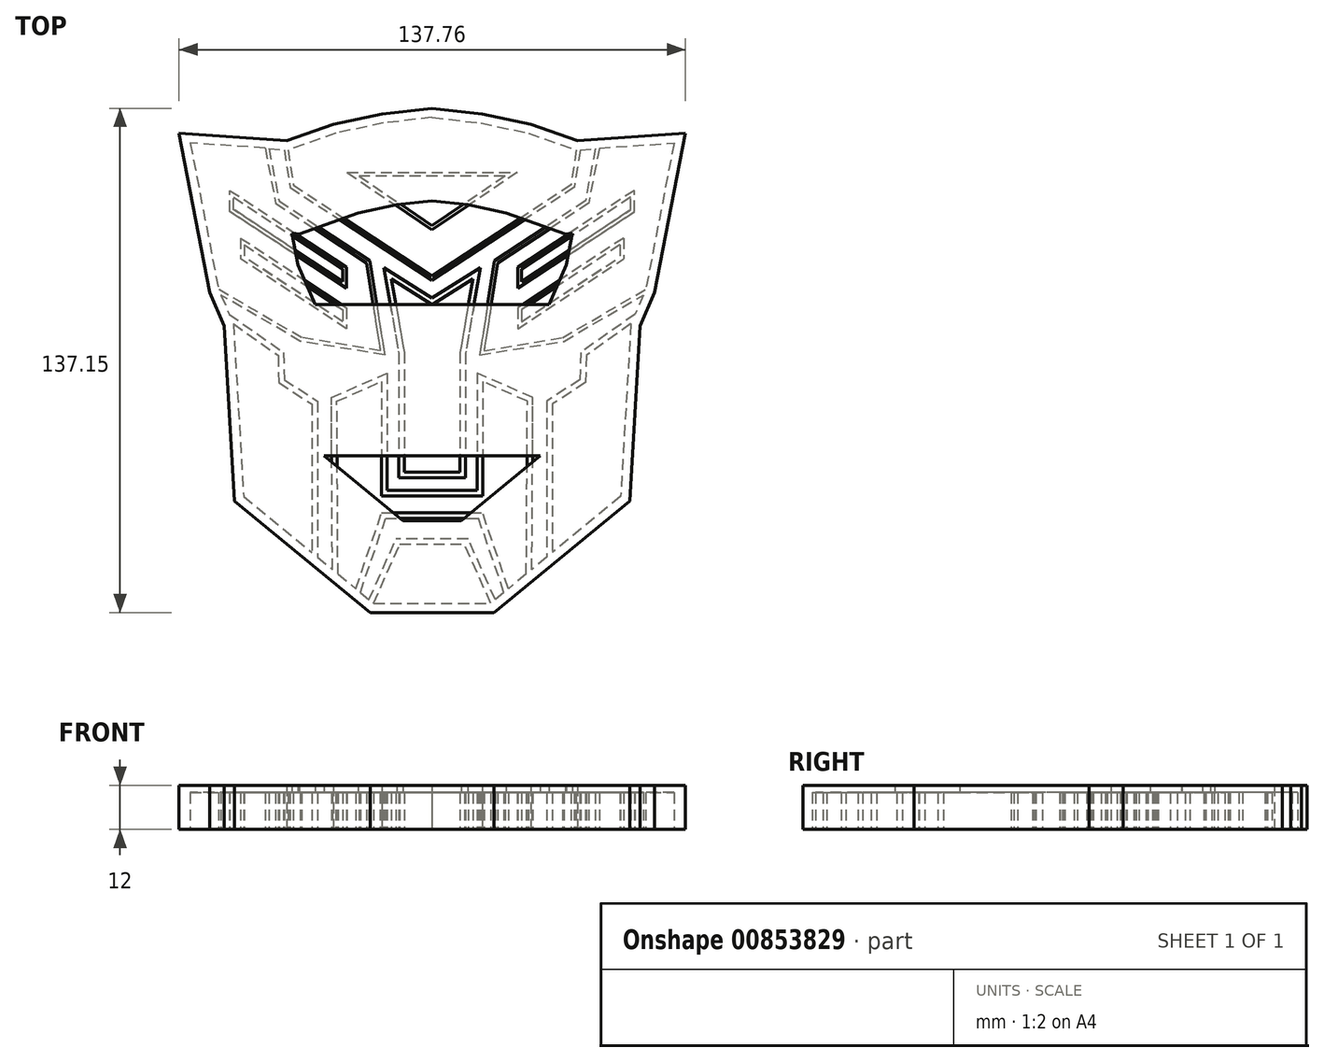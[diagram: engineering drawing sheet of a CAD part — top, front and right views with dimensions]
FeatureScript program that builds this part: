
annotation { "Feature Type Name" : "Feature", "Feature Type Description" : "" }
export const myFeature = defineFeature(function(context is Context, id is Id, definition is map)
    precondition{}
    {
        {
            var Q0;
            Q0=qCreatedBy(makeId("Top.planeOp"),FACE);
            cPlane(context, id + "F0", {"entities" : qUnion([Q0]), "cplaneType" : CPlaneType.OFFSET, "offset" : 2 * mm, "oppositeDirection" : true, "width" : 150 * mm, "height" : 150 * mm});
        }
        {
            var Q0;
            Q0=qCreatedBy(makeId("Top.planeOp"),FACE);
            var sketch = newSketch(context, id + "F1", { "sketchPlane" : qUnion([Q0])});
            skLineSegment(sketch, "E0", {"start": v(0, 70.5) * mm, "end": v(-13.27, 69) * mm});
            skLineSegment(sketch, "E1", {"start": v(-13.27, 69) * mm, "end": v(-26.23, 66.23) * mm});
            skLineSegment(sketch, "E2", {"start": v(-26.23, 66.23) * mm, "end": v(-39.24, 61.65) * mm});
            skLineSegment(sketch, "E3", {"start": v(-65.8, 63.53) * mm, "end": v(-58.11, 23.73) * mm});
            skLineSegment(sketch, "E4", {"start": v(-57.45, 22.2) * mm, "end": v(-55.2, 17) * mm});
            skLineSegment(sketch, "E5", {"start": v(-54.07, 14.36) * mm, "end": v(-51.3, -32.61) * mm});
            skLineSegment(sketch, "E6", {"start": v(-51.3, -32.61) * mm, "end": v(-32.74, -47.85) * mm});
            skLineSegment(sketch, "E7", {"start": v(-15.95, -61.64) * mm, "end": v(0, -61.64) * mm});
            skLineSegment(sketch, "E8.0", {"start": v(-16.84, -64.14) * mm, "end": v(0, -64.14) * mm});
            skLineSegment(sketch, "E8.1", {"start": v(-53.73, -33.85) * mm, "end": v(-16.84, -64.14) * mm});
            skLineSegment(sketch, "E8.2", {"start": v(-56.54, 13.77) * mm, "end": v(-53.73, -33.85) * mm});
            skLineSegment(sketch, "E8.3", {"start": v(-60.52, 23) * mm, "end": v(-56.54, 13.77) * mm});
            skLineSegment(sketch, "E8.4", {"start": v(-68.88, 66.25) * mm, "end": v(-60.52, 23) * mm});
            skLineSegment(sketch, "E8.5", {"start": v(0, 73) * mm, "end": v(-13.67, 71.48) * mm});
            skLineSegment(sketch, "E8.6", {"start": v(-13.67, 71.48) * mm, "end": v(-26.91, 68.64) * mm});
            skLineSegment(sketch, "E8.7", {"start": v(-26.91, 68.64) * mm, "end": v(-39.6, 64.17) * mm});
            skLineSegment(sketch, "E8.8", {"start": v(-39.6, 64.17) * mm, "end": v(-68.88, 66.25) * mm});
            skLineSegment(sketch, "E9", {"start": v(0, 55.54) * mm, "end": v(-23.13, 55.54) * mm});
            skLineSegment(sketch, "E10", {"start": v(-23.13, 55.54) * mm, "end": v(0, 39.93) * mm});
            skLineSegment(sketch, "E11.0", {"start": v(-19.86, 54.54) * mm, "end": v(0, 41.13) * mm});
            skLineSegment(sketch, "E11.1", {"start": v(0, 54.54) * mm, "end": v(-19.86, 54.54) * mm});
            skLineSegment(sketch, "E12", {"start": v(-39.24, 61.65) * mm, "end": v(-37.75, 52.11) * mm});
            skLineSegment(sketch, "E13", {"start": v(-37.75, 52.11) * mm, "end": v(0, 27.37) * mm});
            skLineSegment(sketch, "E14.0", {"start": v(-38.67, 51.52) * mm, "end": v(0, 26.18) * mm});
            skLineSegment(sketch, "E14.1", {"start": v(-40.26, 61.7) * mm, "end": v(-38.67, 51.52) * mm});
            skLineSegment(sketch, "E15", {"start": v(-45.46, 62.21) * mm, "end": v(-42.55, 47.16) * mm});
            skLineSegment(sketch, "E16", {"start": v(-42.55, 47.16) * mm, "end": v(-17.9, 30.94) * mm});
            skLineSegment(sketch, "E17", {"start": v(-17.9, 30.94) * mm, "end": v(-14.13, 7.11) * mm});
            skLineSegment(sketch, "E18", {"start": v(-14.13, 7.11) * mm, "end": v(-35.49, 10.61) * mm});
            skLineSegment(sketch, "E19", {"start": v(-35.49, 10.61) * mm, "end": v(-58.11, 23.73) * mm});
            skLineSegment(sketch, "E20.0", {"start": v(-35.83, 9.65) * mm, "end": v(-57.45, 22.2) * mm});
            skLineSegment(sketch, "E20.1", {"start": v(-44.4, 62) * mm, "end": v(-41.65, 47.76) * mm});
            skLineSegment(sketch, "E20.2", {"start": v(-41.65, 47.76) * mm, "end": v(-16.99, 31.54) * mm});
            skLineSegment(sketch, "E20.3", {"start": v(-16.99, 31.54) * mm, "end": v(-12.93, 5.9) * mm});
            skLineSegment(sketch, "E20.4", {"start": v(-12.93, 5.9) * mm, "end": v(-35.83, 9.65) * mm});
            skLineSegment(sketch, "E21", {"start": v(-54.07, 14.36) * mm, "end": v(-41.9, 5.77) * mm});
            skLineSegment(sketch, "E22", {"start": v(-41.9, 5.77) * mm, "end": v(-41.72, -1.6) * mm});
            skLineSegment(sketch, "E23", {"start": v(-41.72, -1.6) * mm, "end": v(-32.74, -7.47) * mm});
            skLineSegment(sketch, "E24", {"start": v(-32.74, -7.47) * mm, "end": v(-32.74, -47.85) * mm});
            skLineSegment(sketch, "E25.0", {"start": v(-31.24, -6.66) * mm, "end": v(-31.24, -49.08) * mm});
            skLineSegment(sketch, "E25.1", {"start": v(-40.24, -0.78) * mm, "end": v(-31.24, -6.66) * mm});
            skLineSegment(sketch, "E25.2", {"start": v(-40.43, 6.56) * mm, "end": v(-40.24, -0.78) * mm});
            skLineSegment(sketch, "E25.3", {"start": v(-55.2, 17) * mm, "end": v(-40.43, 6.56) * mm});
            skLineSegment(sketch, "E26.trimOffspring", {"start": v(-45.46, 62.21) * mm, "end": v(-65.8, 63.53) * mm});
            skLineSegment(sketch, "E27.trimOffspring", {"start": v(-31.24, -49.08) * mm, "end": v(-27.14, -52.45) * mm});
            skLineSegment(sketch, "E28", {"start": v(-25.63, -53.69) * mm, "end": v(-25.92, -6.67) * mm});
            skLineSegment(sketch, "E29", {"start": v(-25.92, -6.67) * mm, "end": v(-13.73, -1.3) * mm});
            skLineSegment(sketch, "E30", {"start": v(-13.73, -1.3) * mm, "end": v(-13.73, -32.47) * mm});
            skLineSegment(sketch, "E31", {"start": v(-13.73, -32.47) * mm, "end": v(0, -32.47) * mm});
            skLineSegment(sketch, "E32", {"start": v(-20.78, -57.67) * mm, "end": v(-13.73, -37.08) * mm});
            skLineSegment(sketch, "E33", {"start": v(-13.73, -37.08) * mm, "end": v(0, -37.08) * mm});
            skLineSegment(sketch, "E34", {"start": v(-15.95, -61.64) * mm, "end": v(-8.81, -45.58) * mm});
            skLineSegment(sketch, "E35", {"start": v(-8.81, -45.58) * mm, "end": v(0, -45.58) * mm});
            skLineSegment(sketch, "E36.0", {"start": v(-12.23, -30.97) * mm, "end": v(0, -30.97) * mm});
            skLineSegment(sketch, "E36.1", {"start": v(-12.23, 1) * mm, "end": v(-12.23, -30.97) * mm});
            skLineSegment(sketch, "E36.2", {"start": v(-27.42, -5.7) * mm, "end": v(-12.23, 1) * mm});
            skLineSegment(sketch, "E36.3", {"start": v(-27.14, -52.45) * mm, "end": v(-27.42, -5.7) * mm});
            skLineSegment(sketch, "E37.0", {"start": v(-9.79, -44.08) * mm, "end": v(0, -44.08) * mm});
            skLineSegment(sketch, "E37.1", {"start": v(-17.15, -60.65) * mm, "end": v(-9.79, -44.08) * mm});
            skLineSegment(sketch, "E38.0", {"start": v(-12.66, -38.58) * mm, "end": v(0, -38.58) * mm});
            skLineSegment(sketch, "E38.1", {"start": v(-19.54, -58.69) * mm, "end": v(-12.66, -38.58) * mm});
            skLineSegment(sketch, "E39.trimOffspring", {"start": v(-25.63, -53.69) * mm, "end": v(-20.78, -57.67) * mm});
            skLineSegment(sketch, "E40.trimOffspring", {"start": v(-19.54, -58.69) * mm, "end": v(-17.15, -60.65) * mm});
            skLineSegment(sketch, "E41", {"start": v(0, 19.63) * mm, "end": v(-11.13, 26.56) * mm});
            skLineSegment(sketch, "E42", {"start": v(-11.13, 26.56) * mm, "end": v(-7.57, 6.56) * mm});
            skLineSegment(sketch, "E43", {"start": v(-7.57, 6.56) * mm, "end": v(-7.57, -25.95) * mm});
            skLineSegment(sketch, "E44", {"start": v(-7.57, -25.95) * mm, "end": v(0, -25.95) * mm});
            skLineSegment(sketch, "E45.0", {"start": v(-9.07, -27.45) * mm, "end": v(0, -27.45) * mm});
            skLineSegment(sketch, "E45.1", {"start": v(-9.07, 6.43) * mm, "end": v(-9.07, -27.45) * mm});
            skLineSegment(sketch, "E45.2", {"start": v(-13.2, 29.6) * mm, "end": v(-9.07, 6.43) * mm});
            skLineSegment(sketch, "E45.3", {"start": v(0, 21.4) * mm, "end": v(-13.2, 29.6) * mm});
            skLineSegment(sketch, "E46", {"start": v(-55.05, 50.68) * mm, "end": v(-23.28, 29.77) * mm});
            skLineSegment(sketch, "E47", {"start": v(-23.28, 29.77) * mm, "end": v(-23.28, 24.02) * mm});
            skLineSegment(sketch, "E48", {"start": v(-23.28, 24.02) * mm, "end": v(-55.05, 44.92) * mm});
            skLineSegment(sketch, "E49", {"start": v(-55.05, 44.92) * mm, "end": v(-55.05, 50.68) * mm});
            skLineSegment(sketch, "E50.0", {"start": v(-54.05, 45.46) * mm, "end": v(-54.05, 48.82) * mm});
            skLineSegment(sketch, "E50.1", {"start": v(-24.28, 25.87) * mm, "end": v(-54.05, 45.46) * mm});
            skLineSegment(sketch, "E50.2", {"start": v(-24.28, 29.23) * mm, "end": v(-24.28, 25.87) * mm});
            skLineSegment(sketch, "E50.3", {"start": v(-54.05, 48.82) * mm, "end": v(-24.28, 29.23) * mm});
            skLineSegment(sketch, "E51", {"start": v(-52.13, 37.73) * mm, "end": v(-23.28, 18.74) * mm});
            skLineSegment(sketch, "E52", {"start": v(-23.28, 18.74) * mm, "end": v(-23.28, 13.05) * mm});
            skLineSegment(sketch, "E53", {"start": v(-23.28, 13.05) * mm, "end": v(-52.13, 32.04) * mm});
            skLineSegment(sketch, "E54", {"start": v(-52.13, 37.73) * mm, "end": v(-52.13, 32.04) * mm});
            skLineSegment(sketch, "E55.0", {"start": v(-51.13, 35.87) * mm, "end": v(-51.13, 32.58) * mm});
            skLineSegment(sketch, "E55.1", {"start": v(-51.13, 35.87) * mm, "end": v(-24.28, 18.2) * mm});
            skLineSegment(sketch, "E55.2", {"start": v(-24.28, 18.2) * mm, "end": v(-24.28, 14.9) * mm});
            skLineSegment(sketch, "E55.3", {"start": v(-24.28, 14.9) * mm, "end": v(-51.13, 32.58) * mm});
            skLineSegment(sketch, "E56", {"start": v(0, 11.68) * mm, "end": v(0, -12.85) * mm, "construction": true});
            skLineSegment(sketch, "E57.MirrorCS", {"start": v(54.05, 45.46) * mm, "end": v(54.05, 48.82) * mm});
            skLineSegment(sketch, "E58.MirrorCS", {"start": v(51.13, 35.87) * mm, "end": v(51.13, 32.58) * mm});
            skLineSegment(sketch, "E59.MirrorCS", {"start": v(55.05, 44.92) * mm, "end": v(55.05, 50.68) * mm});
            skLineSegment(sketch, "E60.MirrorCS", {"start": v(31.24, -49.08) * mm, "end": v(27.14, -52.45) * mm});
            skLineSegment(sketch, "E61.MirrorCS", {"start": v(23.28, 29.77) * mm, "end": v(23.28, 24.02) * mm});
            skLineSegment(sketch, "E62.MirrorCS", {"start": v(52.13, 37.73) * mm, "end": v(52.13, 32.04) * mm});
            skLineSegment(sketch, "E63.MirrorCS", {"start": v(23.28, 18.74) * mm, "end": v(23.28, 13.05) * mm});
            skLineSegment(sketch, "E64.MirrorCS", {"start": v(57.45, 22.2) * mm, "end": v(55.2, 17) * mm});
            skLineSegment(sketch, "E65.MirrorCS", {"start": v(24.28, 29.23) * mm, "end": v(24.28, 25.87) * mm});
            skLineSegment(sketch, "E66.MirrorCS", {"start": v(19.54, -58.69) * mm, "end": v(17.15, -60.65) * mm});
            skLineSegment(sketch, "E67.MirrorCS", {"start": v(24.28, 18.2) * mm, "end": v(24.28, 14.9) * mm});
            skLineSegment(sketch, "E68.MirrorCS", {"start": v(39.24, 61.65) * mm, "end": v(37.75, 52.11) * mm});
            skLineSegment(sketch, "E69.MirrorCS", {"start": v(9.07, -27.45) * mm, "end": v(0, -27.45) * mm});
            skLineSegment(sketch, "E70.MirrorCS", {"start": v(17.9, 30.94) * mm, "end": v(14.13, 7.11) * mm});
            skLineSegment(sketch, "E71.MirrorCS", {"start": v(15.95, -61.64) * mm, "end": v(8.81, -45.58) * mm});
            skLineSegment(sketch, "E72.MirrorCS", {"start": v(17.15, -60.65) * mm, "end": v(9.79, -44.08) * mm});
            skLineSegment(sketch, "E73.MirrorCS", {"start": v(55.2, 17) * mm, "end": v(40.43, 6.56) * mm});
            skLineSegment(sketch, "E74.MirrorCS", {"start": v(42.55, 47.16) * mm, "end": v(17.9, 30.94) * mm});
            skLineSegment(sketch, "E75.MirrorCS", {"start": v(0, 70.5) * mm, "end": v(13.27, 69) * mm});
            skLineSegment(sketch, "E76.MirrorCS", {"start": v(26.91, 68.64) * mm, "end": v(39.6, 64.17) * mm});
            skLineSegment(sketch, "E77.MirrorCS", {"start": v(12.66, -38.58) * mm, "end": v(0, -38.58) * mm});
            skLineSegment(sketch, "E78.MirrorCS", {"start": v(25.63, -53.69) * mm, "end": v(25.92, -6.67) * mm});
            skLineSegment(sketch, "E79.MirrorCS", {"start": v(45.46, 62.21) * mm, "end": v(65.8, 63.53) * mm});
            skLineSegment(sketch, "E80.MirrorCS", {"start": v(0, 73) * mm, "end": v(13.67, 71.48) * mm});
            skLineSegment(sketch, "E81.MirrorCS", {"start": v(13.67, 71.48) * mm, "end": v(26.91, 68.64) * mm});
            skLineSegment(sketch, "E82.MirrorCS", {"start": v(8.81, -45.58) * mm, "end": v(0, -45.58) * mm});
            skLineSegment(sketch, "E83.MirrorCS", {"start": v(41.9, 5.77) * mm, "end": v(41.72, -1.6) * mm});
            skLineSegment(sketch, "E84.MirrorCS", {"start": v(35.49, 10.61) * mm, "end": v(58.11, 23.73) * mm});
            skLineSegment(sketch, "E85.MirrorCS", {"start": v(0, 54.54) * mm, "end": v(19.86, 54.54) * mm});
            skLineSegment(sketch, "E86.MirrorCS", {"start": v(24.28, 25.87) * mm, "end": v(54.05, 45.46) * mm});
            skLineSegment(sketch, "E87.MirrorCS", {"start": v(19.54, -58.69) * mm, "end": v(12.66, -38.58) * mm});
            skLineSegment(sketch, "E88.MirrorCS", {"start": v(25.92, -6.67) * mm, "end": v(13.73, -1.3) * mm});
            skLineSegment(sketch, "E89.MirrorCS", {"start": v(13.27, 69) * mm, "end": v(26.23, 66.23) * mm});
            skLineSegment(sketch, "E90.MirrorCS", {"start": v(41.72, -1.6) * mm, "end": v(32.74, -7.47) * mm});
            skLineSegment(sketch, "E91.MirrorCS", {"start": v(12.23, -30.97) * mm, "end": v(0, -30.97) * mm});
            skLineSegment(sketch, "E92.MirrorCS", {"start": v(26.23, 66.23) * mm, "end": v(39.24, 61.65) * mm});
            skLineSegment(sketch, "E93.MirrorCS", {"start": v(54.07, 14.36) * mm, "end": v(51.3, -32.61) * mm});
            skLineSegment(sketch, "E94.MirrorCS", {"start": v(27.14, -52.45) * mm, "end": v(27.42, -5.7) * mm});
            skLineSegment(sketch, "E95.MirrorCS", {"start": v(40.24, -0.78) * mm, "end": v(31.24, -6.66) * mm});
            skLineSegment(sketch, "E96.MirrorCS", {"start": v(39.6, 64.17) * mm, "end": v(68.88, 66.25) * mm});
            skLineSegment(sketch, "E97.MirrorCS", {"start": v(41.65, 47.76) * mm, "end": v(16.99, 31.54) * mm});
            skLineSegment(sketch, "E98.MirrorCS", {"start": v(9.07, 6.43) * mm, "end": v(9.07, -27.45) * mm});
            skLineSegment(sketch, "E99.MirrorCS", {"start": v(7.57, -25.95) * mm, "end": v(0, -25.95) * mm});
            skLineSegment(sketch, "E100.MirrorCS", {"start": v(14.13, 7.11) * mm, "end": v(35.49, 10.61) * mm});
            skLineSegment(sketch, "E101.MirrorCS", {"start": v(51.3, -32.61) * mm, "end": v(32.74, -47.85) * mm});
            skLineSegment(sketch, "E102.MirrorCS", {"start": v(23.13, 55.54) * mm, "end": v(0, 39.93) * mm});
            skLineSegment(sketch, "E103.MirrorCS", {"start": v(12.93, 5.9) * mm, "end": v(35.83, 9.65) * mm});
            skLineSegment(sketch, "E104.MirrorCS", {"start": v(40.43, 6.56) * mm, "end": v(40.24, -0.78) * mm});
            skLineSegment(sketch, "E105.MirrorCS", {"start": v(54.07, 14.36) * mm, "end": v(41.9, 5.77) * mm});
            skLineSegment(sketch, "E106.MirrorCS", {"start": v(9.79, -44.08) * mm, "end": v(0, -44.08) * mm});
            skLineSegment(sketch, "E107.MirrorCS", {"start": v(13.73, -37.08) * mm, "end": v(0, -37.08) * mm});
            skLineSegment(sketch, "E108.MirrorCS", {"start": v(19.86, 54.54) * mm, "end": v(0, 41.13) * mm});
            skLineSegment(sketch, "E109.MirrorCS", {"start": v(45.46, 62.21) * mm, "end": v(42.55, 47.16) * mm});
            skLineSegment(sketch, "E110.MirrorCS", {"start": v(23.28, 24.02) * mm, "end": v(55.05, 44.92) * mm});
            skLineSegment(sketch, "E111.MirrorCS", {"start": v(40.26, 61.7) * mm, "end": v(38.67, 51.52) * mm});
            skLineSegment(sketch, "E112.MirrorCS", {"start": v(16.84, -64.14) * mm, "end": v(0, -64.14) * mm});
            skLineSegment(sketch, "E113.MirrorCS", {"start": v(35.83, 9.65) * mm, "end": v(57.45, 22.2) * mm});
            skLineSegment(sketch, "E114.MirrorCS", {"start": v(25.63, -53.69) * mm, "end": v(20.78, -57.67) * mm});
            skLineSegment(sketch, "E115.MirrorCS", {"start": v(23.28, 13.05) * mm, "end": v(52.13, 32.04) * mm});
            skLineSegment(sketch, "E116.MirrorCS", {"start": v(65.8, 63.53) * mm, "end": v(58.11, 23.73) * mm});
            skLineSegment(sketch, "E117.MirrorCS", {"start": v(0, 19.63) * mm, "end": v(11.13, 26.56) * mm});
            skLineSegment(sketch, "E118.MirrorCS", {"start": v(0, 21.4) * mm, "end": v(13.2, 29.6) * mm});
            skLineSegment(sketch, "E119.MirrorCS", {"start": v(13.73, -1.3) * mm, "end": v(13.73, -32.47) * mm});
            skLineSegment(sketch, "E120.MirrorCS", {"start": v(11.13, 26.56) * mm, "end": v(7.57, 6.56) * mm});
            skLineSegment(sketch, "E121.MirrorCS", {"start": v(32.74, -7.47) * mm, "end": v(32.74, -47.85) * mm});
            skLineSegment(sketch, "E122.MirrorCS", {"start": v(37.75, 52.11) * mm, "end": v(0, 27.37) * mm});
            skLineSegment(sketch, "E123.MirrorCS", {"start": v(52.13, 37.73) * mm, "end": v(23.28, 18.74) * mm});
            skLineSegment(sketch, "E124.MirrorCS", {"start": v(12.23, 1) * mm, "end": v(12.23, -30.97) * mm});
            skLineSegment(sketch, "E125.MirrorCS", {"start": v(54.05, 48.82) * mm, "end": v(24.28, 29.23) * mm});
            skLineSegment(sketch, "E126.MirrorCS", {"start": v(15.95, -61.64) * mm, "end": v(0, -61.64) * mm});
            skLineSegment(sketch, "E127.MirrorCS", {"start": v(24.28, 14.9) * mm, "end": v(51.13, 32.58) * mm});
            skLineSegment(sketch, "E128.MirrorCS", {"start": v(56.54, 13.77) * mm, "end": v(53.73, -33.85) * mm});
            skLineSegment(sketch, "E129.MirrorCS", {"start": v(44.4, 62) * mm, "end": v(41.65, 47.76) * mm});
            skLineSegment(sketch, "E130.MirrorCS", {"start": v(16.99, 31.54) * mm, "end": v(12.93, 5.9) * mm});
            skLineSegment(sketch, "E131.MirrorCS", {"start": v(0, 55.54) * mm, "end": v(23.13, 55.54) * mm});
            skLineSegment(sketch, "E132.MirrorCS", {"start": v(7.57, 6.56) * mm, "end": v(7.57, -25.95) * mm});
            skLineSegment(sketch, "E133.MirrorCS", {"start": v(53.73, -33.85) * mm, "end": v(16.84, -64.14) * mm});
            skLineSegment(sketch, "E134.MirrorCS", {"start": v(38.67, 51.52) * mm, "end": v(0, 26.18) * mm});
            skLineSegment(sketch, "E135.MirrorCS", {"start": v(20.78, -57.67) * mm, "end": v(13.73, -37.08) * mm});
            skLineSegment(sketch, "E136.MirrorCS", {"start": v(13.2, 29.6) * mm, "end": v(9.07, 6.43) * mm});
            skLineSegment(sketch, "E137.MirrorCS", {"start": v(55.05, 50.68) * mm, "end": v(23.28, 29.77) * mm});
            skLineSegment(sketch, "E138.MirrorCS", {"start": v(68.88, 66.25) * mm, "end": v(60.52, 23) * mm});
            skLineSegment(sketch, "E139.MirrorCS", {"start": v(13.73, -32.47) * mm, "end": v(0, -32.47) * mm});
            skLineSegment(sketch, "E140.MirrorCS", {"start": v(31.24, -6.66) * mm, "end": v(31.24, -49.08) * mm});
            skLineSegment(sketch, "E141.MirrorCS", {"start": v(60.52, 23) * mm, "end": v(56.54, 13.77) * mm});
            skLineSegment(sketch, "E142.MirrorCS", {"start": v(51.13, 35.87) * mm, "end": v(24.28, 18.2) * mm});
            skLineSegment(sketch, "E143.MirrorCS", {"start": v(27.42, -5.7) * mm, "end": v(12.23, 1) * mm});
            skPoint(sketch, "E144.orphan", {"position": v(0.8, 20.9) * mm});
            skPoint(sketch, "E145.orphan", {"position": v(-0.8, 20.9) * mm});
            skPoint(sketch, "E146.orphan", {"position": v(0.66, 40.69) * mm});
            skPoint(sketch, "E147.orphan", {"position": v(-0.66, 40.69) * mm});
            skPoint(sketch, "E148.orphan", {"position": v(0.84, 26.73) * mm});
            skPoint(sketch, "E149.orphan", {"position": v(-0.84, 26.73) * mm});
            skLineSegment(sketch, "E150", {"start": v(40.26, 61.7) * mm, "end": v(44.4, 62) * mm});
            skLineSegment(sketch, "E151", {"start": v(-44.4, 62) * mm, "end": v(-40.26, 61.7) * mm});
            skSolve(sketch);
        }
        {
            var Q0;
            Q0=makeQuery(id+"F1.imprint","IMPRINT",FACE,{"disambiguationData":[TD([[makeQuery(id+"F1.imprint","IMPRINT",EDGE,{"derivedFrom":sQuery(id+"F1.wireOp",EDGE,"E0")}),-1.0]])]});
            var Q1;
            Q1=makeQuery(id+"F1.imprint","IMPRINT",FACE,{"disambiguationData":[TD([[makeQuery(id+"F1.imprint","IMPRINT",EDGE,{"derivedFrom":sQuery(id+"F1.wireOp",EDGE,"E9")}),1.0]])]});
            var Q2;
            Q2=makeQuery(id+"F1.imprint","IMPRINT",FACE,{"disambiguationData":[TD([[makeQuery(id+"F1.imprint","IMPRINT",EDGE,{"derivedFrom":sQuery(id+"F1.wireOp",EDGE,"E46")}),-1.0]])]});
            var Q3;
            Q3=makeQuery(id+"F1.imprint","IMPRINT",FACE,{"disambiguationData":[TD([[makeQuery(id+"F1.imprint","IMPRINT",EDGE,{"derivedFrom":sQuery(id+"F1.wireOp",EDGE,"E51")}),-1.0]])]});
            var Q4;
            Q4=makeQuery(id+"F1.imprint","IMPRINT",FACE,{"disambiguationData":[TD([[makeQuery(id+"F1.imprint","IMPRINT",EDGE,{"derivedFrom":sQuery(id+"F1.wireOp",EDGE,"E57.MirrorCS")}),-1.0]])]});
            var Q5;
            Q5=makeQuery(id+"F1.imprint","IMPRINT",FACE,{"disambiguationData":[TD([[makeQuery(id+"F1.imprint","IMPRINT",EDGE,{"derivedFrom":sQuery(id+"F1.wireOp",EDGE,"E58.MirrorCS")}),1.0]])]});
            var Q6;
            Q6=makeQuery(id+"F1.imprint","IMPRINT",FACE,{"disambiguationData":[TD([[makeQuery(id+"F1.imprint","IMPRINT",EDGE,{"derivedFrom":sQuery(id+"F1.wireOp",EDGE,"E41")}),-1.0]])]});
            extrude(context, id + "F2", {"entities" : qUnion([Q0, Q1, Q2, Q3, Q4, Q5, Q6]), "depth" : 10 * mm, "offsetDistance" : 25 * mm});
        }
        {
            var Q0;
            Q0=makeQuery(id+"F2.opExtrude","CAP_FACE",FACE,{"disambiguationData":[OSD([sQuery(id+"F1.wireOp",EDGE,"E0"),sQuery(id+"F1.wireOp",EDGE,"E1"),sQuery(id+"F1.wireOp",EDGE,"E2"),sQuery(id+"F1.wireOp",EDGE,"E3"),sQuery(id+"F1.wireOp",EDGE,"E4"),sQuery(id+"F1.wireOp",EDGE,"E5"),sQuery(id+"F1.wireOp",EDGE,"E6"),sQuery(id+"F1.wireOp",EDGE,"E7"),sQuery(id+"F1.wireOp",EDGE,"E8.0"),sQuery(id+"F1.wireOp",EDGE,"E8.1"),sQuery(id+"F1.wireOp",EDGE,"E8.2"),sQuery(id+"F1.wireOp",EDGE,"E8.3"),sQuery(id+"F1.wireOp",EDGE,"E8.4"),sQuery(id+"F1.wireOp",EDGE,"E8.5"),sQuery(id+"F1.wireOp",EDGE,"E8.6"),sQuery(id+"F1.wireOp",EDGE,"E8.7"),sQuery(id+"F1.wireOp",EDGE,"E8.8"),sQuery(id+"F1.wireOp",EDGE,"E12"),sQuery(id+"F1.wireOp",EDGE,"E13"),sQuery(id+"F1.wireOp",EDGE,"E14.0"),sQuery(id+"F1.wireOp",EDGE,"E14.1"),sQuery(id+"F1.wireOp",EDGE,"E15"),sQuery(id+"F1.wireOp",EDGE,"E16"),sQuery(id+"F1.wireOp",EDGE,"E17"),sQuery(id+"F1.wireOp",EDGE,"E18"),sQuery(id+"F1.wireOp",EDGE,"E19"),sQuery(id+"F1.wireOp",EDGE,"E20.0"),sQuery(id+"F1.wireOp",EDGE,"E20.1"),sQuery(id+"F1.wireOp",EDGE,"E20.2"),sQuery(id+"F1.wireOp",EDGE,"E20.3"),sQuery(id+"F1.wireOp",EDGE,"E20.4"),sQuery(id+"F1.wireOp",EDGE,"E21"),sQuery(id+"F1.wireOp",EDGE,"E22"),sQuery(id+"F1.wireOp",EDGE,"E23"),sQuery(id+"F1.wireOp",EDGE,"E24"),sQuery(id+"F1.wireOp",EDGE,"E25.0"),sQuery(id+"F1.wireOp",EDGE,"E25.1"),sQuery(id+"F1.wireOp",EDGE,"E25.2"),sQuery(id+"F1.wireOp",EDGE,"E25.3"),sQuery(id+"F1.wireOp",EDGE,"E26.trimOffspring"),sQuery(id+"F1.wireOp",EDGE,"E27.trimOffspring"),sQuery(id+"F1.wireOp",EDGE,"E28"),sQuery(id+"F1.wireOp",EDGE,"E29"),sQuery(id+"F1.wireOp",EDGE,"E30"),sQuery(id+"F1.wireOp",EDGE,"E31"),sQuery(id+"F1.wireOp",EDGE,"E32"),sQuery(id+"F1.wireOp",EDGE,"E33"),sQuery(id+"F1.wireOp",EDGE,"E34"),sQuery(id+"F1.wireOp",EDGE,"E35"),sQuery(id+"F1.wireOp",EDGE,"E36.0"),sQuery(id+"F1.wireOp",EDGE,"E36.1"),sQuery(id+"F1.wireOp",EDGE,"E36.2"),sQuery(id+"F1.wireOp",EDGE,"E36.3"),sQuery(id+"F1.wireOp",EDGE,"E37.0"),sQuery(id+"F1.wireOp",EDGE,"E37.1"),sQuery(id+"F1.wireOp",EDGE,"E38.0"),sQuery(id+"F1.wireOp",EDGE,"E38.1"),sQuery(id+"F1.wireOp",EDGE,"E39.trimOffspring"),sQuery(id+"F1.wireOp",EDGE,"E40.trimOffspring"),sQuery(id+"F1.wireOp",EDGE,"E60.MirrorCS"),sQuery(id+"F1.wireOp",EDGE,"E64.MirrorCS"),sQuery(id+"F1.wireOp",EDGE,"E66.MirrorCS"),sQuery(id+"F1.wireOp",EDGE,"E68.MirrorCS"),sQuery(id+"F1.wireOp",EDGE,"E70.MirrorCS"),sQuery(id+"F1.wireOp",EDGE,"E71.MirrorCS"),sQuery(id+"F1.wireOp",EDGE,"E72.MirrorCS"),sQuery(id+"F1.wireOp",EDGE,"E73.MirrorCS"),sQuery(id+"F1.wireOp",EDGE,"E74.MirrorCS"),sQuery(id+"F1.wireOp",EDGE,"E75.MirrorCS"),sQuery(id+"F1.wireOp",EDGE,"E76.MirrorCS"),sQuery(id+"F1.wireOp",EDGE,"E77.MirrorCS"),sQuery(id+"F1.wireOp",EDGE,"E78.MirrorCS"),sQuery(id+"F1.wireOp",EDGE,"E79.MirrorCS"),sQuery(id+"F1.wireOp",EDGE,"E80.MirrorCS"),sQuery(id+"F1.wireOp",EDGE,"E81.MirrorCS"),sQuery(id+"F1.wireOp",EDGE,"E82.MirrorCS"),sQuery(id+"F1.wireOp",EDGE,"E83.MirrorCS"),sQuery(id+"F1.wireOp",EDGE,"E84.MirrorCS"),sQuery(id+"F1.wireOp",EDGE,"E87.MirrorCS"),sQuery(id+"F1.wireOp",EDGE,"E88.MirrorCS"),sQuery(id+"F1.wireOp",EDGE,"E89.MirrorCS"),sQuery(id+"F1.wireOp",EDGE,"E90.MirrorCS"),sQuery(id+"F1.wireOp",EDGE,"E91.MirrorCS"),sQuery(id+"F1.wireOp",EDGE,"E92.MirrorCS"),sQuery(id+"F1.wireOp",EDGE,"E93.MirrorCS"),sQuery(id+"F1.wireOp",EDGE,"E94.MirrorCS"),sQuery(id+"F1.wireOp",EDGE,"E95.MirrorCS"),sQuery(id+"F1.wireOp",EDGE,"E96.MirrorCS"),sQuery(id+"F1.wireOp",EDGE,"E97.MirrorCS"),sQuery(id+"F1.wireOp",EDGE,"E100.MirrorCS"),sQuery(id+"F1.wireOp",EDGE,"E101.MirrorCS"),sQuery(id+"F1.wireOp",EDGE,"E103.MirrorCS"),sQuery(id+"F1.wireOp",EDGE,"E104.MirrorCS"),sQuery(id+"F1.wireOp",EDGE,"E105.MirrorCS"),sQuery(id+"F1.wireOp",EDGE,"E106.MirrorCS"),sQuery(id+"F1.wireOp",EDGE,"E107.MirrorCS"),sQuery(id+"F1.wireOp",EDGE,"E109.MirrorCS"),sQuery(id+"F1.wireOp",EDGE,"E111.MirrorCS"),sQuery(id+"F1.wireOp",EDGE,"E112.MirrorCS"),sQuery(id+"F1.wireOp",EDGE,"E113.MirrorCS"),sQuery(id+"F1.wireOp",EDGE,"E114.MirrorCS"),sQuery(id+"F1.wireOp",EDGE,"E116.MirrorCS"),sQuery(id+"F1.wireOp",EDGE,"E119.MirrorCS"),sQuery(id+"F1.wireOp",EDGE,"E121.MirrorCS"),sQuery(id+"F1.wireOp",EDGE,"E122.MirrorCS"),sQuery(id+"F1.wireOp",EDGE,"E124.MirrorCS"),sQuery(id+"F1.wireOp",EDGE,"E126.MirrorCS"),sQuery(id+"F1.wireOp",EDGE,"E128.MirrorCS"),sQuery(id+"F1.wireOp",EDGE,"E129.MirrorCS"),sQuery(id+"F1.wireOp",EDGE,"E130.MirrorCS"),sQuery(id+"F1.wireOp",EDGE,"E133.MirrorCS"),sQuery(id+"F1.wireOp",EDGE,"E134.MirrorCS"),sQuery(id+"F1.wireOp",EDGE,"E135.MirrorCS"),sQuery(id+"F1.wireOp",EDGE,"E138.MirrorCS"),sQuery(id+"F1.wireOp",EDGE,"E139.MirrorCS"),sQuery(id+"F1.wireOp",EDGE,"E140.MirrorCS"),sQuery(id+"F1.wireOp",EDGE,"E141.MirrorCS"),sQuery(id+"F1.wireOp",EDGE,"E143.MirrorCS"),sQuery(id+"F1.wireOp",EDGE,"E150"),sQuery(id+"F1.wireOp",EDGE,"E151")])],"isStart":false});
            var sketch = newSketch(context, id + "F3", { "sketchPlane" : qUnion([Q0])});
            skLineSegment(sketch, "E152.0", {"start": v(-39.6, 64.17) * mm, "end": v(-68.88, 66.25) * mm});
            skLineSegment(sketch, "E153.0", {"start": v(-68.88, 66.25) * mm, "end": v(-60.52, 23) * mm});
            skLineSegment(sketch, "E154.0", {"start": v(-60.52, 23) * mm, "end": v(-56.54, 13.77) * mm});
            skLineSegment(sketch, "E155.0", {"start": v(-56.54, 13.77) * mm, "end": v(-53.73, -33.85) * mm});
            skLineSegment(sketch, "E156.0", {"start": v(-53.73, -33.85) * mm, "end": v(-16.84, -64.14) * mm});
            skLineSegment(sketch, "E157.0", {"start": v(-16.84, -64.14) * mm, "end": v(16.84, -64.14) * mm});
            skLineSegment(sketch, "E158.0", {"start": v(56.54, 13.77) * mm, "end": v(53.73, -33.85) * mm});
            skLineSegment(sketch, "E159.0", {"start": v(60.52, 23) * mm, "end": v(56.54, 13.77) * mm});
            skLineSegment(sketch, "E160.0", {"start": v(68.88, 66.25) * mm, "end": v(60.52, 23) * mm});
            skLineSegment(sketch, "E161.0", {"start": v(39.6, 64.17) * mm, "end": v(68.88, 66.25) * mm});
            skLineSegment(sketch, "E162.0", {"start": v(26.91, 68.64) * mm, "end": v(39.6, 64.17) * mm});
            skPoint(sketch, "E163.0", {"position": v(20.3, 70.06) * mm});
            skLineSegment(sketch, "E164.0", {"start": v(0, 73) * mm, "end": v(13.67, 71.48) * mm});
            skPoint(sketch, "E165.0", {"position": v(-6.83, 72.24) * mm});
            skLineSegment(sketch, "E166.0", {"start": v(-13.67, 71.48) * mm, "end": v(-26.91, 68.64) * mm});
            skLineSegment(sketch, "E167.0", {"start": v(53.73, -33.85) * mm, "end": v(16.84, -64.14) * mm});
            skLineSegment(sketch, "E168.0", {"start": v(13.67, 71.48) * mm, "end": v(26.91, 68.64) * mm});
            skLineSegment(sketch, "E169.0", {"start": v(0, 73) * mm, "end": v(-13.67, 71.48) * mm});
            skLineSegment(sketch, "E170.0", {"start": v(-26.91, 68.64) * mm, "end": v(-39.6, 64.17) * mm});
            skLineSegment(sketch, "E171.0", {"start": v(-20.11, 44.53) * mm, "end": v(-36.2, 38.87) * mm});
            skLineSegment(sketch, "E171.1", {"start": v(-9.65, 46.77) * mm, "end": v(-20.11, 44.53) * mm});
            skLineSegment(sketch, "E171.2", {"start": v(0, 47.85) * mm, "end": v(-9.65, 46.77) * mm});
            skLineSegment(sketch, "E171.3", {"start": v(0, 47.85) * mm, "end": v(9.65, 46.77) * mm});
            skLineSegment(sketch, "E171.4", {"start": v(9.65, 46.77) * mm, "end": v(20.11, 44.53) * mm});
            skLineSegment(sketch, "E171.5", {"start": v(-36.2, 38.87) * mm, "end": v(-38.15, 39) * mm});
            skLineSegment(sketch, "E171.6", {"start": v(20.11, 44.53) * mm, "end": v(36.2, 38.87) * mm});
            skLineSegment(sketch, "E171.7", {"start": v(-29.41, -21.47) * mm, "end": v(-7.9, -39.14) * mm});
            skLineSegment(sketch, "E171.9", {"start": v(-36.49, 30.4) * mm, "end": v(-31.84, 19.64) * mm});
            skLineSegment(sketch, "E171.10", {"start": v(-38.15, 39) * mm, "end": v(-36.49, 30.4) * mm});
            skLineSegment(sketch, "E171.11", {"start": v(-7.9, -39.14) * mm, "end": v(7.9, -39.14) * mm});
            skLineSegment(sketch, "E171.12", {"start": v(29.41, -21.47) * mm, "end": v(7.9, -39.14) * mm});
            skLineSegment(sketch, "E171.14", {"start": v(36.49, 30.4) * mm, "end": v(31.84, 19.64) * mm});
            skLineSegment(sketch, "E171.15", {"start": v(38.15, 39) * mm, "end": v(36.49, 30.4) * mm});
            skLineSegment(sketch, "E171.16", {"start": v(36.2, 38.87) * mm, "end": v(38.15, 39) * mm});
            skLineSegment(sketch, "E172", {"start": v(-31.84, 19.64) * mm, "end": v(31.84, 19.64) * mm});
            skLineSegment(sketch, "E173", {"start": v(-29.41, -21.47) * mm, "end": v(29.41, -21.47) * mm});
            skSolve(sketch);
        }
        {
            var Q0;
            Q0=qSketchRegion(id+"F3",true);
            extrude(context, id + "F4", {"entities" : qUnion([Q0]), "operationType" : NewBodyOperationType.ADD, "depth" : 2 * mm, "offsetDistance" : 25 * mm});
        }
    });
